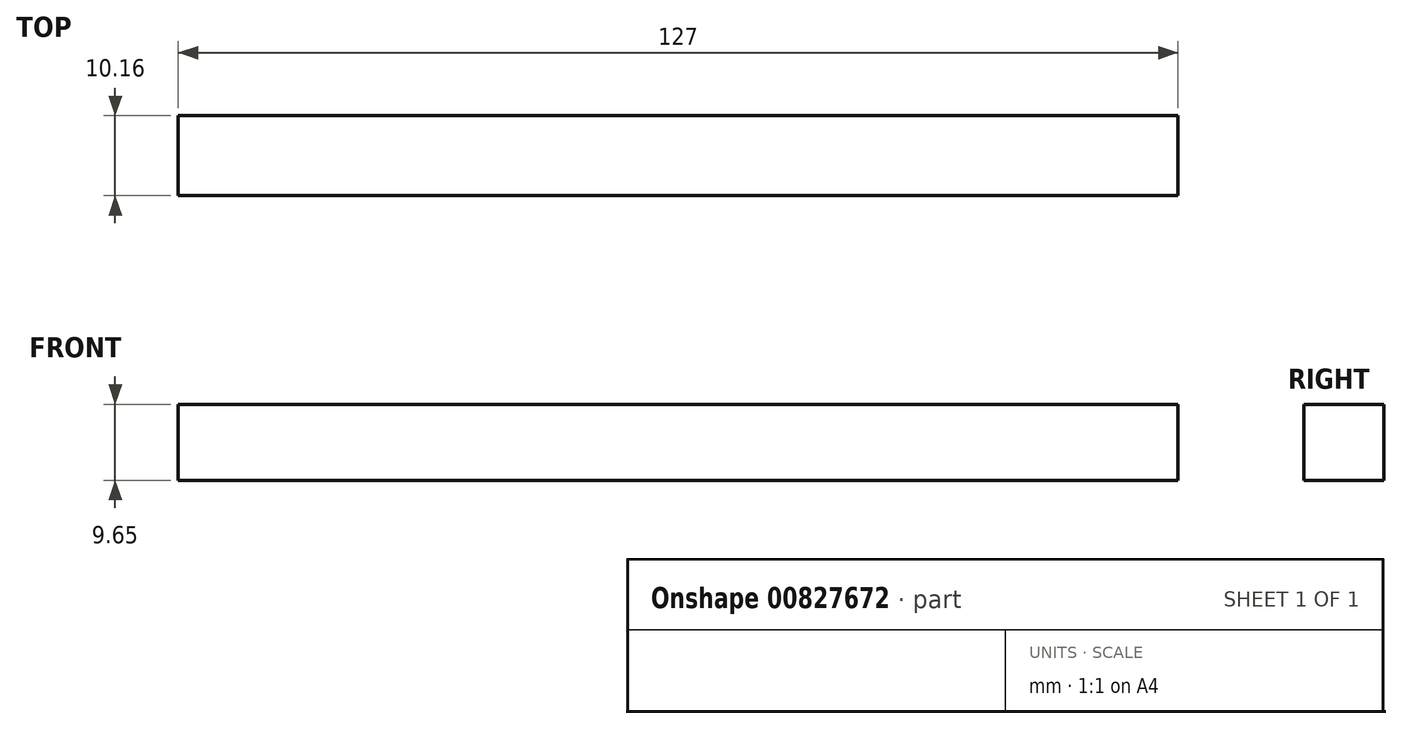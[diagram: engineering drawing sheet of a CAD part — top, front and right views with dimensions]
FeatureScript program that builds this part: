
annotation { "Feature Type Name" : "Feature", "Feature Type Description" : "" }
export const myFeature = defineFeature(function(context is Context, id is Id, definition is map)
    precondition{}
    {
        {
            var Q0;
            Q0=qCreatedBy(makeId("Top.planeOp"),FACE);
            var sketch = newSketch(context, id + "F0", { "sketchPlane" : qUnion([Q0])});
            skLineSegment(sketch, "E0.bottom", {"start": v(-63.5, 5.08) * mm, "end": v(63.5, 5.08) * mm});
            skLineSegment(sketch, "E0.top", {"start": v(-63.5, -5.08) * mm, "end": v(63.5, -5.08) * mm});
            skLineSegment(sketch, "E0.left", {"start": v(-63.5, 5.08) * mm, "end": v(-63.5, -5.08) * mm});
            skLineSegment(sketch, "E0.right", {"start": v(63.5, 5.08) * mm, "end": v(63.5, -5.08) * mm});
            skPoint(sketch, "E0.middle", {"position": v(0, 0) * mm});
            skSolve(sketch);
        }
        {
            var Q0;
            Q0 = qSketchRegion(id + "F0", true);
            extrude(context, id + "F1", {"entities" : qUnion([Q0]), "depth" : 9.65 * mm, "offsetDistance" : 25.4 * mm});
        }
    });
